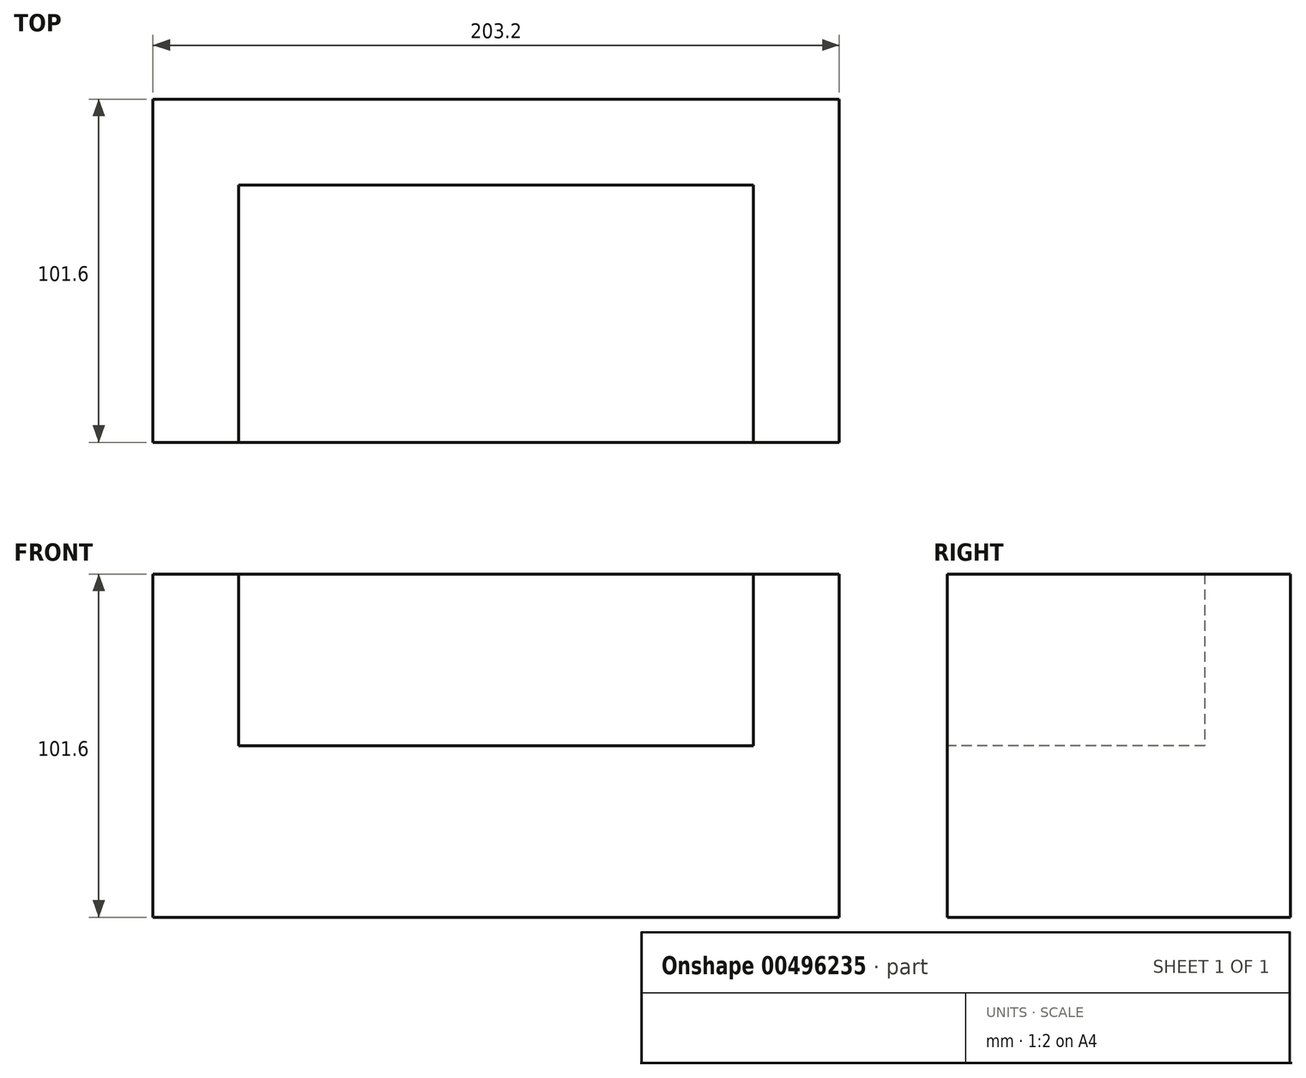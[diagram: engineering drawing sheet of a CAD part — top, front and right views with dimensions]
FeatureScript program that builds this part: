
annotation { "Feature Type Name" : "Feature", "Feature Type Description" : "" }
export const myFeature = defineFeature(function(context is Context, id is Id, definition is map)
    precondition{}
    {
        {
            var Q0;
            Q0=qCreatedBy(makeId("Front.planeOp"),FACE);
            var sketch = newSketch(context, id + "F0", { "sketchPlane" : qUnion([Q0])});
            skLineSegment(sketch, "E0.bottom", {"start": v(0, 0) * mm, "end": v(101.6, 0) * mm});
            skLineSegment(sketch, "E0.top", {"start": v(0, 101.6) * mm, "end": v(101.6, 101.6) * mm});
            skLineSegment(sketch, "E0.left", {"start": v(0, 0) * mm, "end": v(0, 101.6) * mm});
            skLineSegment(sketch, "E0.right", {"start": v(101.6, 0) * mm, "end": v(101.6, 101.6) * mm});
            skSolve(sketch);
        }
        {
            var Q0;
            Q0 = qSketchRegion(id + "F0", true);
            extrude(context, id + "F1", {"entities" : qUnion([Q0]), "depth" : 203.2 * mm});
        }
        {
            var Q0;
            Q0=makeQuery(id+"F1.opExtrude","SWEPT_FACE",FACE,{"disambiguationData":[OSD([sQuery(id+"F0.wireOp",EDGE,"E0.left")])]});
            var sketch = newSketch(context, id + "F2", { "sketchPlane" : qUnion([Q0])});
            skLineSegment(sketch, "E1", {"start": v(0, 101.6) * mm, "end": v(25.4, 101.6) * mm});
            skLineSegment(sketch, "E2.bottom", {"start": v(25.4, 101.6) * mm, "end": v(177.8, 101.6) * mm});
            skLineSegment(sketch, "E2.top", {"start": v(25.4, 50.8) * mm, "end": v(177.8, 50.8) * mm});
            skLineSegment(sketch, "E2.left", {"start": v(25.4, 101.6) * mm, "end": v(25.4, 50.8) * mm});
            skLineSegment(sketch, "E2.right", {"start": v(177.8, 101.6) * mm, "end": v(177.8, 50.8) * mm});
            skSolve(sketch);
        }
        {
            var Q0;
            Q0 = qSketchRegion(id + "F2", true);
            extrude(context, id + "F3", {"entities" : qUnion([Q0]), "operationType" : NewBodyOperationType.REMOVE, "oppositeDirection" : true, "depth" : 76.2 * mm});
        }
        {
            var Q0;
            Q0=makeQuery(id+"F1.opExtrude","SWEPT_BODY",BODY,{"disambiguationData":[OSD([sQuery(id+"F0.wireOp",EDGE,"E0.bottom"),sQuery(id+"F0.wireOp",EDGE,"E0.top"),sQuery(id+"F0.wireOp",EDGE,"E0.left"),sQuery(id+"F0.wireOp",EDGE,"E0.right")])]});
            var Q1;
            Q1=makeQuery(id+"F1.opExtrude","CAP_EDGE",EDGE,{"disambiguationData":[OSD([sQuery(id+"F0.wireOp",EDGE,"E0.right")])],"isStart":false});
            transform(context, id + "F4", {"entities" : qUnion([Q0]), "transformType" : TransformType.ROTATION, "transformAxis" : qUnion([Q1]), "angle" : 90 * degree, "makeCopy" : false});
        }
    });
